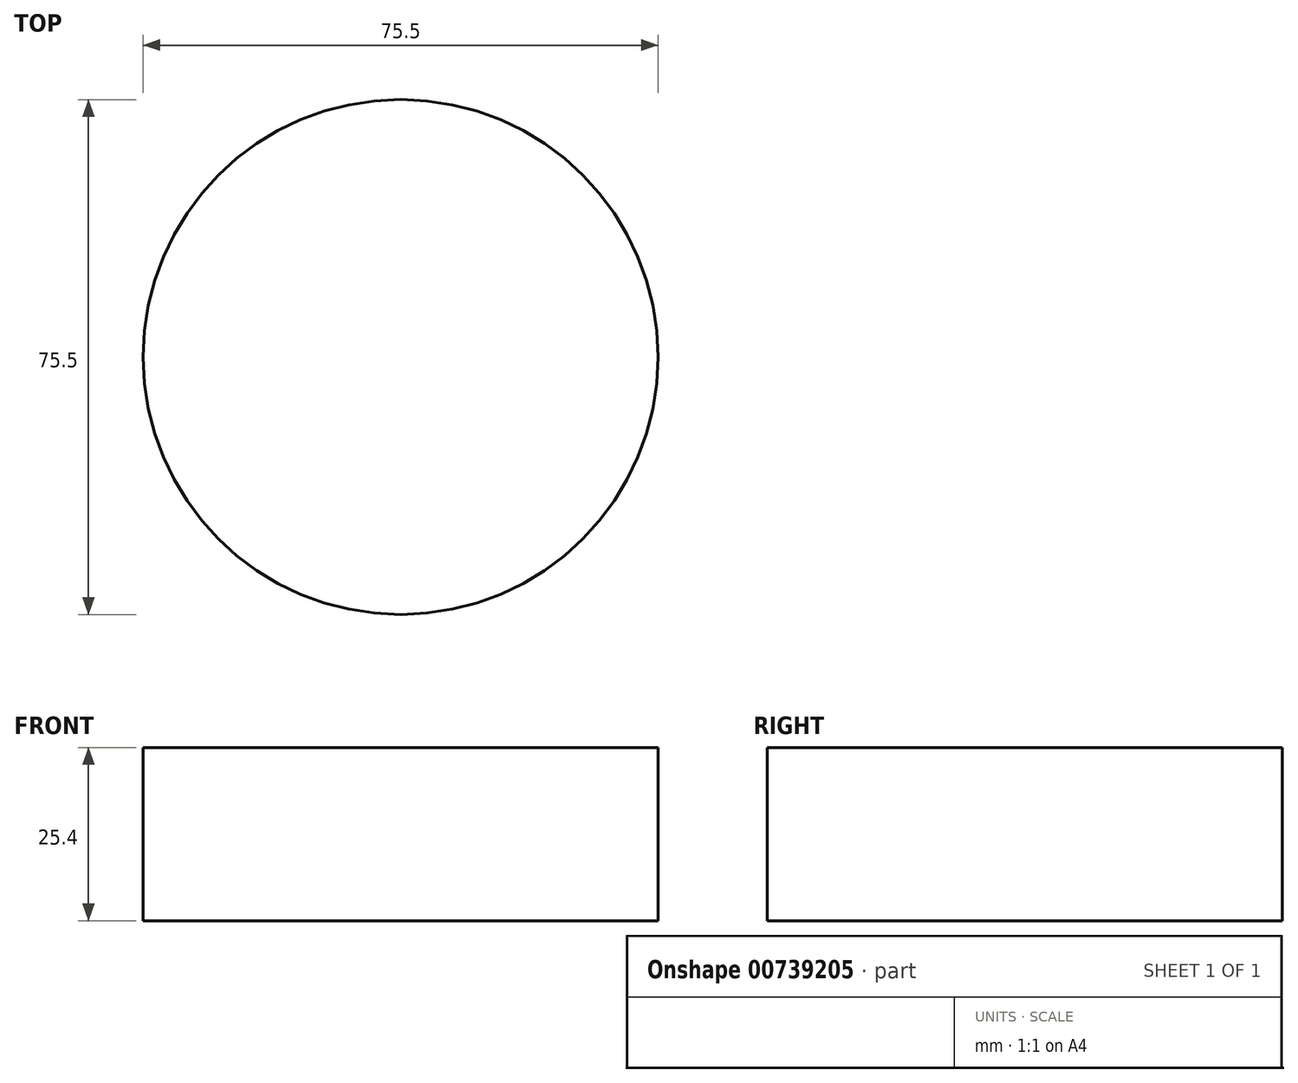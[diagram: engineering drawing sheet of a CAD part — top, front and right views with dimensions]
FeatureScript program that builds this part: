
annotation { "Feature Type Name" : "Feature", "Feature Type Description" : "" }
export const myFeature = defineFeature(function(context is Context, id is Id, definition is map)
    precondition{}
    {
        {
            var Q0;
            Q0=qCreatedBy(makeId("Top.planeOp"),FACE);
            var sketch = newSketch(context, id + "F0", { "sketchPlane" : qUnion([Q0])});
            skCircle(sketch, "E0", {"center": v(0, 0) * mm, "radius": 37.75 * mm});
            skSolve(sketch);
        }
        {
            var Q0;
            Q0 = qSketchRegion(id + "F0", true);
            extrude(context, id + "F1", {"entities" : qUnion([Q0]), "depth" : 25.4 * mm, "offsetDistance" : 25.4 * mm});
        }
    });
